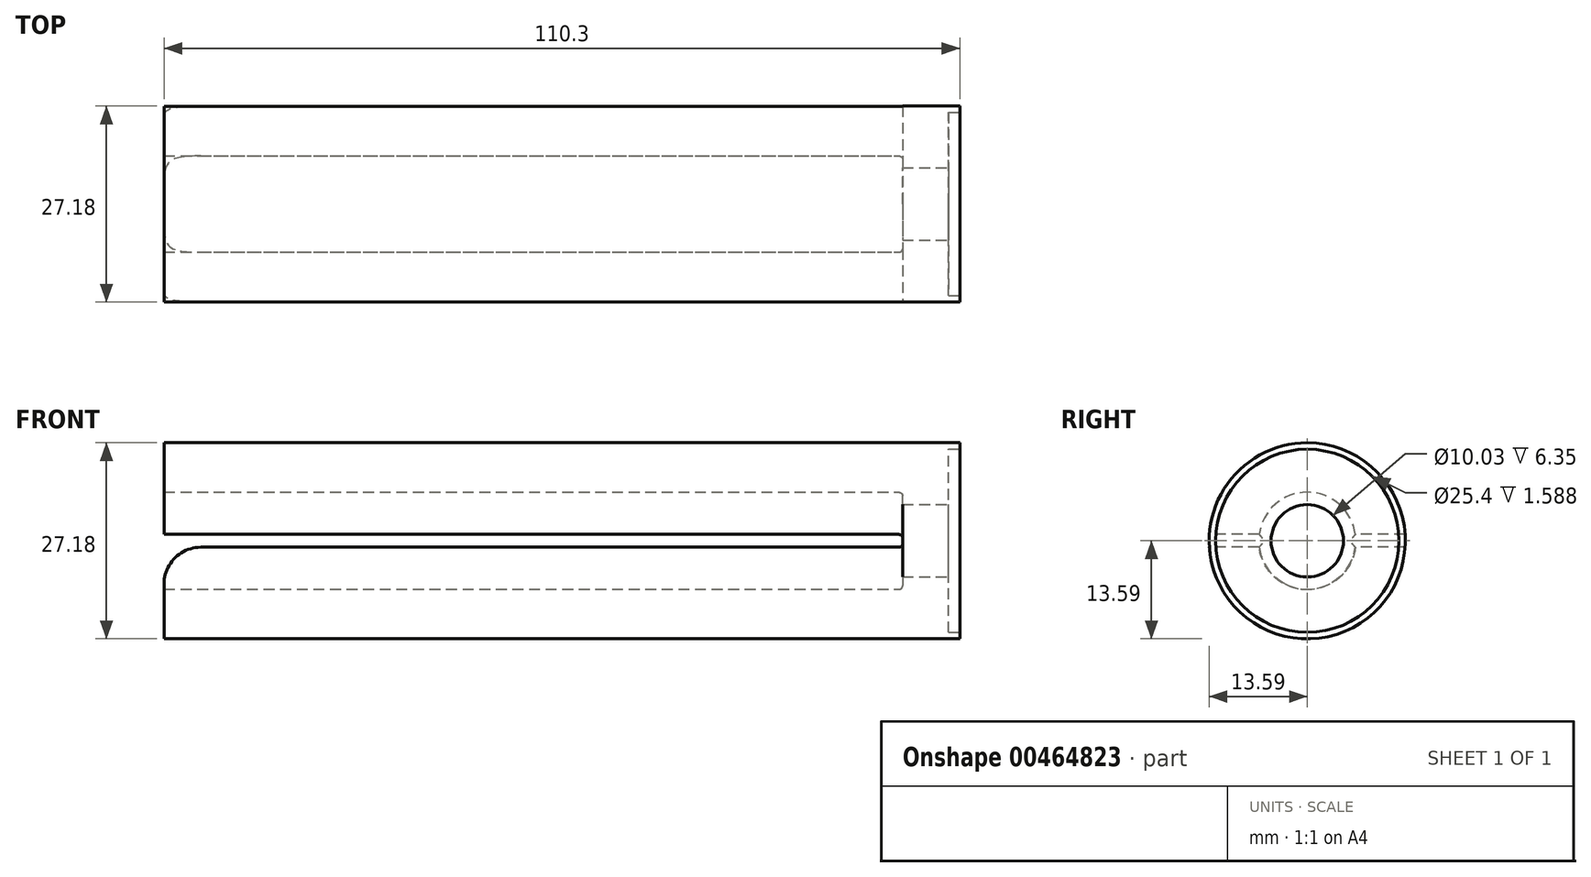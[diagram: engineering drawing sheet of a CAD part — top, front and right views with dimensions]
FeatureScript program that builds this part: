
annotation { "Feature Type Name" : "Feature", "Feature Type Description" : "" }
export const myFeature = defineFeature(function(context is Context, id is Id, definition is map)
    precondition{}
    {
        {
            var Q0;
            Q0=qCreatedBy(makeId("Right.planeOp"),FACE);
            var sketch = newSketch(context, id + "F0", { "sketchPlane" : qUnion([Q0])});
            skCircle(sketch, "E0", {"center": v(0, 0) * mm, "radius": 13.59 * mm});
            skSolve(sketch);
        }
        {
            var Q0;
            Q0 = qSketchRegion(id + "F0", true);
            extrude(context, id + "F1", {"entities" : qUnion([Q0]), "oppositeDirection" : true, "depth" : 114.3 * mm, "offsetDistance" : 25.4 * mm});
        }
        {
            var Q0;
            Q0=qCreatedBy(makeId("Front.planeOp"),FACE);
            var sketch = newSketch(context, id + "F2", { "sketchPlane" : qUnion([Q0])});
            skLineSegment(sketch, "E1.bottom", {"start": v(-5.08, 0.89) * mm, "end": v(-114.3, 0.89) * mm, "construction": true});
            skLineSegment(sketch, "E1.top", {"start": v(-5.08, -0.89) * mm, "end": v(-114.3, -0.89) * mm, "construction": true});
            skLineSegment(sketch, "E1.left", {"start": v(-5.08, 0.89) * mm, "end": v(-5.08, -0.89) * mm, "construction": true});
            skLineSegment(sketch, "E1.right", {"start": v(-114.3, 0.89) * mm, "end": v(-114.3, -0.89) * mm});
            skPoint(sketch, "E1.middle", {"position": v(-59.7, 0) * mm});
            skLineSegment(sketch, "E2", {"start": v(-11.94, 0.89) * mm, "end": v(-11.94, -0.89) * mm, "construction": true});
            skLineSegment(sketch, "E3", {"start": v(-114.3, 0.89) * mm, "end": v(-11.94, 0.89) * mm});
            skLineSegment(sketch, "E4", {"start": v(-11.94, 0.89) * mm, "end": v(-11.94, 0) * mm});
            skLineSegment(sketch, "E5", {"start": v(-11.94, 0) * mm, "end": v(-11.94, -0.89) * mm});
            skLineSegment(sketch, "E6", {"start": v(-11.94, -0.89) * mm, "end": v(-114.3, -0.89) * mm});
            skSolve(sketch);
        }
        {
            var Q0;
            Q0 = qSketchRegion(id + "F2", true);
            extrude(context, id + "F3", {"entities" : qUnion([Q0]), "operationType" : NewBodyOperationType.REMOVE, "endBound" : BoundingType.SYMMETRIC, "oppositeDirection" : true, "depth" : 101.1 * mm});
        }
        {
            var Q0;
            Q0=makeQuery(id+"F1.opExtrude","CAP_FACE",FACE,{"disambiguationData":[OSD([sQuery(id+"F0.wireOp",EDGE,"E0")])],"isStart":true});
            var sketch = newSketch(context, id + "F4", { "sketchPlane" : qUnion([Q0])});
            skCircle(sketch, "E7", {"center": v(0, 0) * mm, "radius": 5.02 * mm});
            skSolve(sketch);
        }
        {
            var Q0;
            Q0 = qSketchRegion(id + "F4", true);
            extrude(context, id + "F5", {"entities" : qUnion([Q0]), "operationType" : NewBodyOperationType.REMOVE, "oppositeDirection" : true, "depth" : 152.4 * mm, "offsetDistance" : 25.4 * mm});
        }
        {
            var Q0;
            Q0=makeQuery(id+"F5.boolean.opBoolean","SPLIT",FACE,{"disambiguationData":[OD(0.0)],"derivedFrom":makeQuery(id+"F3.boolean.opBoolean","COPY",FACE,{"derivedFrom":makeQuery(id+"F3.opExtrude","SWEPT_FACE",FACE,{"disambiguationData":[OSD([sQuery(id+"F2.wireOp",EDGE,"E4"),sQuery(id+"F2.wireOp",EDGE,"E5")])]})})});
            var sketch = newSketch(context, id + "F6", { "sketchPlane" : qUnion([Q0])});
            skCircle(sketch, "E8", {"center": v(0, 0) * mm, "radius": 6.73 * mm});
            skSolve(sketch);
        }
        {
            var Q0;
            Q0 = qSketchRegion(id + "F6", true);
            extrude(context, id + "F7", {"entities" : qUnion([Q0]), "operationType" : NewBodyOperationType.REMOVE, "depth" : 106.93 * mm, "offsetDistance" : 25.4 * mm});
        }
        {
            var Q0;
            Q0=makeQuery(id+"F5.boolean.opBoolean","SPLIT",EDGE,{"disambiguationData":[OD(1.0)],"derivedFrom":makeQuery(id+"F3.boolean.opBoolean","COPY",EDGE,{"derivedFrom":makeQuery(id+"F3.opExtrude","SWEPT_EDGE",EDGE,{"disambiguationData":[OSD([sQuery(id+"F2.wireOp",EDGE,"E1.right"),sQuery(id+"F2.wireOp",EDGE,"E3")])]})})});
            var Q1;
            Q1=makeQuery(id+"F5.boolean.opBoolean","SPLIT",EDGE,{"disambiguationData":[OD(1.0)],"derivedFrom":makeQuery(id+"F3.boolean.opBoolean","COPY",EDGE,{"derivedFrom":makeQuery(id+"F3.opExtrude","SWEPT_EDGE",EDGE,{"disambiguationData":[OSD([sQuery(id+"F2.wireOp",EDGE,"E1.right"),sQuery(id+"F2.wireOp",EDGE,"E6")])]})})});
            var Q2;
            Q2=makeQuery(id+"F5.boolean.opBoolean","SPLIT",EDGE,{"disambiguationData":[OD(0.0)],"derivedFrom":makeQuery(id+"F3.boolean.opBoolean","COPY",EDGE,{"derivedFrom":makeQuery(id+"F3.opExtrude","SWEPT_EDGE",EDGE,{"disambiguationData":[OSD([sQuery(id+"F2.wireOp",EDGE,"E1.right"),sQuery(id+"F2.wireOp",EDGE,"E6")])]})})});
            var Q3;
            Q3=makeQuery(id+"F5.boolean.opBoolean","SPLIT",EDGE,{"disambiguationData":[OD(0.0)],"derivedFrom":makeQuery(id+"F3.boolean.opBoolean","COPY",EDGE,{"derivedFrom":makeQuery(id+"F3.opExtrude","SWEPT_EDGE",EDGE,{"disambiguationData":[OSD([sQuery(id+"F2.wireOp",EDGE,"E1.right"),sQuery(id+"F2.wireOp",EDGE,"E3")])]})})});
            fillet(context, id + "F8", {"entities" : qUnion([Q0, Q1, Q2, Q3]), "radius" : 5.08 * mm, "tangentPropagation" : true, "allowEdgeOverflow" : false});
        }
        {
            var Q0;
            Q0=makeQuery(id+"F5.boolean.opBoolean","SPLIT",EDGE,{"disambiguationData":[OD(1.0)],"derivedFrom":makeQuery(id+"F3.boolean.opBoolean","COPY",EDGE,{"derivedFrom":makeQuery(id+"F3.opExtrude","SWEPT_EDGE",EDGE,{"disambiguationData":[OSD([sQuery(id+"F2.wireOp",EDGE,"E3"),sQuery(id+"F2.wireOp",EDGE,"E4")])]})})});
            var Q1;
            Q1=makeQuery(id+"F5.boolean.opBoolean","SPLIT",EDGE,{"disambiguationData":[OD(1.0)],"derivedFrom":makeQuery(id+"F3.boolean.opBoolean","COPY",EDGE,{"derivedFrom":makeQuery(id+"F3.opExtrude","SWEPT_EDGE",EDGE,{"disambiguationData":[OSD([sQuery(id+"F2.wireOp",EDGE,"E5"),sQuery(id+"F2.wireOp",EDGE,"E6")])]})})});
            var Q2;
            Q2=makeQuery(id+"F5.boolean.opBoolean","SPLIT",EDGE,{"disambiguationData":[OD(0.0)],"derivedFrom":makeQuery(id+"F3.boolean.opBoolean","COPY",EDGE,{"derivedFrom":makeQuery(id+"F3.opExtrude","SWEPT_EDGE",EDGE,{"disambiguationData":[OSD([sQuery(id+"F2.wireOp",EDGE,"E3"),sQuery(id+"F2.wireOp",EDGE,"E4")])]})})});
            var Q3;
            Q3=makeQuery(id+"F5.boolean.opBoolean","SPLIT",EDGE,{"disambiguationData":[OD(0.0)],"derivedFrom":makeQuery(id+"F3.boolean.opBoolean","COPY",EDGE,{"derivedFrom":makeQuery(id+"F3.opExtrude","SWEPT_EDGE",EDGE,{"disambiguationData":[OSD([sQuery(id+"F2.wireOp",EDGE,"E5"),sQuery(id+"F2.wireOp",EDGE,"E6")])]})})});
            var Q4;
            {var subQ0=sQuery(id+"F6.wireOp",EDGE,"E8");Q4=makeQuery(id+"F7.boolean.opBoolean","COPY",EDGE,{"disambiguationData":[TD([makeQuery(id+"F3.boolean.opBoolean","COPY",FACE,{"derivedFrom":makeQuery(id+"F3.opExtrude","SWEPT_FACE",FACE,{"disambiguationData":[OSD([sQuery(id+"F2.wireOp",EDGE,"E3")])]})})])],"derivedFrom":makeQuery(id+"F7.opExtrude","CAP_EDGE",EDGE,{"disambiguationData":[OSD([subQ0])],"isStart":true})});}
            var Q5;
            {var subQ0=sQuery(id+"F6.wireOp",EDGE,"E8");Q5=makeQuery(id+"F7.boolean.opBoolean","COPY",EDGE,{"disambiguationData":[TD([makeQuery(id+"F3.boolean.opBoolean","COPY",FACE,{"derivedFrom":makeQuery(id+"F3.opExtrude","SWEPT_FACE",FACE,{"disambiguationData":[OSD([sQuery(id+"F2.wireOp",EDGE,"E6")])]})})])],"derivedFrom":makeQuery(id+"F7.opExtrude","CAP_EDGE",EDGE,{"disambiguationData":[OSD([subQ0])],"isStart":true})});}
            fillet(context, id + "F9", {"entities" : qUnion([Q0, Q1, Q2, Q3, Q4, Q5]), "radius" : 0.5 * mm, "tangentPropagation" : true, "allowEdgeOverflow" : false});
        }
        {
            var Q0;
            Q0=qCreatedBy(makeId("Front.planeOp"),FACE);
            var sketch = newSketch(context, id + "F10", { "sketchPlane" : qUnion([Q0])});
            skLineSegment(sketch, "E9.bottom", {"start": v(4, 21.04) * mm, "end": v(-4, 21.04) * mm});
            skLineSegment(sketch, "E9.top", {"start": v(4, -21.04) * mm, "end": v(-4, -21.04) * mm});
            skLineSegment(sketch, "E9.left", {"start": v(4, 21.04) * mm, "end": v(4, -21.04) * mm});
            skLineSegment(sketch, "E9.right", {"start": v(-4, 21.04) * mm, "end": v(-4, -21.04) * mm});
            skPoint(sketch, "E9.middle", {"position": v(0, 0) * mm});
            skSolve(sketch);
        }
        {
            var Q0;
            Q0 = qSketchRegion(id + "F10", true);
            extrude(context, id + "F11", {"entities" : qUnion([Q0]), "operationType" : NewBodyOperationType.REMOVE, "endBound" : BoundingType.SYMMETRIC, "oppositeDirection" : true, "depth" : 35.66 * mm, "offsetDistance" : 25.4 * mm});
        }
        {
            var Q0;
            Q0=makeQuery(id+"F11.boolean.opBoolean","COPY",FACE,{"derivedFrom":makeQuery(id+"F11.opExtrude","SWEPT_FACE",FACE,{"disambiguationData":[OSD([sQuery(id+"F10.wireOp",EDGE,"E9.right")])]})});
            var sketch = newSketch(context, id + "F12", { "sketchPlane" : qUnion([Q0])});
            skCircle(sketch, "E10", {"center": v(0, 0) * mm, "radius": 12.7 * mm});
            skSolve(sketch);
        }
        {
            var Q0;
            Q0 = qSketchRegion(id + "F12", true);
            extrude(context, id + "F13", {"entities" : qUnion([Q0]), "operationType" : NewBodyOperationType.REMOVE, "oppositeDirection" : true, "depth" : 1.59 * mm, "offsetDistance" : 25.4 * mm});
        }
    });
